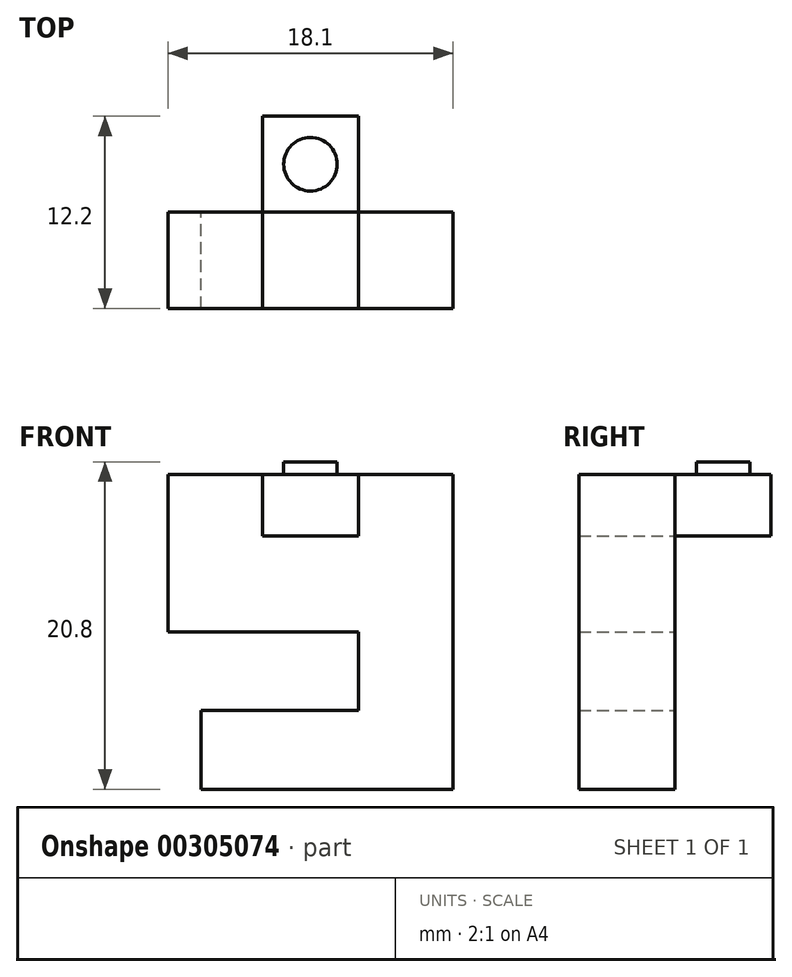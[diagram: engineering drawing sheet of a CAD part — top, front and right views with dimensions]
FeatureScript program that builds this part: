
annotation { "Feature Type Name" : "Feature", "Feature Type Description" : "" }
export const myFeature = defineFeature(function(context is Context, id is Id, definition is map)
    precondition{}
    {
        {
            var Q0;
            Q0=qCreatedBy(makeId("Front.planeOp"),FACE);
            var sketch = newSketch(context, id + "F0", { "sketchPlane" : qUnion([Q0])});
            skLineSegment(sketch, "E0.bottom", {"start": v(0, 0) * mm, "end": v(6.1, 0) * mm});
            skLineSegment(sketch, "E0.top", {"start": v(0, 3.9) * mm, "end": v(6.1, 3.9) * mm});
            skLineSegment(sketch, "E0.left", {"start": v(0, 0) * mm, "end": v(0, 3.9) * mm});
            skLineSegment(sketch, "E0.right", {"start": v(6.1, 0) * mm, "end": v(6.1, 3.9) * mm});
            skSolve(sketch);
        }
        {
            var Q0;
            Q0=makeQuery(id+"F0.imprint","IMPRINT",FACE,{"disambiguationData":[TD([[makeQuery(id+"F0.imprint","IMPRINT",EDGE,{"derivedFrom":sQuery(id+"F0.wireOp",EDGE,"E0.bottom")}),1.0]])]});
            extrude(context, id + "F1", {"entities" : qUnion([Q0]), "depth" : 6.1 * mm});
        }
        {
            var Q0;
            Q0=makeQuery(id+"F1.opExtrude","SWEPT_FACE",FACE,{"disambiguationData":[OSD([sQuery(id+"F0.wireOp",EDGE,"E0.top")])]});
            var sketch = newSketch(context, id + "F2", { "sketchPlane" : qUnion([Q0])});
            skCircle(sketch, "E1", {"center": v(3.05, -3.05) * mm, "radius": 1.7 * mm});
            skSolve(sketch);
        }
        {
            var Q0;
            Q0 = qSketchRegion(id + "F2", true);
            extrude(context, id + "F3", {"entities" : qUnion([Q0]), "operationType" : NewBodyOperationType.ADD, "depth" : 0.8 * mm});
        }
        {
            var Q0;
            Q0=makeQuery(id+"F1.opExtrude","CAP_FACE",FACE,{"disambiguationData":[OSD([sQuery(id+"F0.wireOp",EDGE,"E0.bottom"),sQuery(id+"F0.wireOp",EDGE,"E0.top"),sQuery(id+"F0.wireOp",EDGE,"E0.left"),sQuery(id+"F0.wireOp",EDGE,"E0.right")])],"isStart":false});
            var sketch = newSketch(context, id + "F4", { "sketchPlane" : qUnion([Q0])});
            skLineSegment(sketch, "E2.bottom", {"start": v(0, 3.9) * mm, "end": v(-6, 3.9) * mm});
            skLineSegment(sketch, "E2.top", {"start": v(0, -6.1) * mm, "end": v(-6, -6.1) * mm});
            skLineSegment(sketch, "E2.left", {"start": v(0, 3.9) * mm, "end": v(0, -6.1) * mm});
            skLineSegment(sketch, "E2.right", {"start": v(-6, 3.9) * mm, "end": v(-6, -6.1) * mm});
            skLineSegment(sketch, "E3.bottom", {"start": v(6.1, 3.9) * mm, "end": v(12.1, 3.9) * mm});
            skLineSegment(sketch, "E3.top", {"start": v(6.1, -6.1) * mm, "end": v(12.1, -6.1) * mm});
            skLineSegment(sketch, "E3.left", {"start": v(6.1, 3.9) * mm, "end": v(6.1, -6.1) * mm});
            skLineSegment(sketch, "E3.right", {"start": v(12.1, 3.9) * mm, "end": v(12.1, -6.1) * mm});
            skLineSegment(sketch, "E4.bottom", {"start": v(0, 0) * mm, "end": v(6.1, 0) * mm});
            skLineSegment(sketch, "E4.top", {"start": v(0, -6.1) * mm, "end": v(6.1, -6.1) * mm});
            skLineSegment(sketch, "E4.left", {"start": v(0, 0) * mm, "end": v(0, -6.1) * mm});
            skLineSegment(sketch, "E4.right", {"start": v(6.1, 0) * mm, "end": v(6.1, -6.1) * mm});
            skLineSegment(sketch, "E5.bottom", {"start": v(12.1, -6.1) * mm, "end": v(6.1, -6.1) * mm});
            skLineSegment(sketch, "E5.top", {"start": v(12.1, -16.1) * mm, "end": v(6.1, -16.1) * mm});
            skLineSegment(sketch, "E5.left", {"start": v(12.1, -6.1) * mm, "end": v(12.1, -16.1) * mm});
            skLineSegment(sketch, "E5.right", {"start": v(6.1, -6.1) * mm, "end": v(6.1, -16.1) * mm});
            skLineSegment(sketch, "E6.bottom", {"start": v(6.1, -16.1) * mm, "end": v(-3.9, -16.1) * mm});
            skLineSegment(sketch, "E6.top", {"start": v(6.1, -11.1) * mm, "end": v(-3.9, -11.1) * mm});
            skLineSegment(sketch, "E6.left", {"start": v(6.1, -16.1) * mm, "end": v(6.1, -11.1) * mm});
            skLineSegment(sketch, "E6.right", {"start": v(-3.9, -16.1) * mm, "end": v(-3.9, -11.1) * mm});
            skSolve(sketch);
        }
        {
            var Q0;
            Q0 = qSketchRegion(id + "F4", true);
            extrude(context, id + "F5", {"entities" : qUnion([Q0]), "depth" : 6.1 * mm});
        }
    });
